annotation { "Feature Type Name" : "Feature", "Feature Type Description" : "" }
export const myFeature = defineFeature(function(context is Context, id is Id, definition is map)
    precondition{}
    {
        {
            var Q0;
            Q0=qCreatedBy(makeId("Top.planeOp"),FACE);
            var sketch = newSketch(context, id + "F0", { "sketchPlane" : qUnion([Q0])});
            skLineSegment(sketch, "E0.bottom", {"start": v(50.8, 25.4) * mm, "end": v(-50.8, 25.4) * mm});
            skLineSegment(sketch, "E0.top", {"start": v(50.8, -25.4) * mm, "end": v(-50.8, -25.4) * mm});
            skLineSegment(sketch, "E0.left", {"start": v(50.8, 25.4) * mm, "end": v(50.8, -25.4) * mm});
            skLineSegment(sketch, "E0.right", {"start": v(-50.8, 25.4) * mm, "end": v(-50.8, -25.4) * mm});
            skPoint(sketch, "E0.middle", {"position": v(0, 0) * mm});
            skSolve(sketch);
        }
        {
            var Q0;
            Q0=makeQuery(id+"F0.imprint","IMPRINT",FACE,{"disambiguationData":[TD([[makeQuery(id+"F0.imprint","IMPRINT",EDGE,{"derivedFrom":sQuery(id+"F0.wireOp",EDGE,"E0.bottom")}),1.0]])]});
            var Q1;
            Q1 = qSketchRegion(id + "F2", true);
            extrude(context, id + "F1", {"entities" : qUnion([Q0, Q1]), "depth" : 6.35 * mm, "offsetDistance" : 25.4 * mm});
        }
        {
            var Q0;
            Q0=makeQuery(id+"F1.opExtrude","CAP_FACE",FACE,{"disambiguationData":[OSD([sQuery(id+"F0.wireOp",EDGE,"E0.bottom"),sQuery(id+"F0.wireOp",EDGE,"E0.top"),sQuery(id+"F0.wireOp",EDGE,"E0.left"),sQuery(id+"F0.wireOp",EDGE,"E0.right")])],"isStart":false});
            var sketch = newSketch(context, id + "F2", { "sketchPlane" : qUnion([Q0])});
            skText(sketch, "E1", { "text": "Michael De Tata", "fontName": "OpenSans-Bold.ttf"});
            const initialGuessF2  = {"E1": [-0.04472, 0.0108, 1, 0, 0.00818]};
            skSetInitialGuess(sketch, initialGuessF2);
            skSolve(sketch);
        }
        {
            var Q0;
            Q0=makeQuery(id+"F2.imprint","IMPRINT",FACE,{"disambiguationData":[TD([[makeQuery(id+"F2.imprint","IMPRINT",EDGE,{"derivedFrom":sQuery(id+"F2.wireOp",EDGE,"E1.sketch_text.stroke-0")}),1.0]])]});
            var sketch = newSketch(context, id + "F3", { "sketchPlane" : qUnion([Q0])});
            skCircle(sketch, "E2", {"center": v(-29.02, -8) * mm, "radius": 11.12 * mm});
            skArc(sketch, "E3", {"start": v(-35.55, 0) * mm, "mid": v(-39.34, -7.67) * mm, "end": v(-36.05, -15.56) * mm});
            skArc(sketch, "E4", {"start": v(-36.05, -15.56) * mm, "mid": v(-35.35, -14.88) * mm, "end": v(-34.72, -14.14) * mm});
            skArc(sketch, "E5", {"start": v(-35.25, -16.23) * mm, "mid": v(-34.54, -15.43) * mm, "end": v(-33.9, -14.58) * mm});
            skArc(sketch, "E6", {"start": v(-22.4, -0.07) * mm, "mid": v(-22.9, -0.63) * mm, "end": v(-23.36, -1.22) * mm});
            skArc(sketch, "E7", {"start": v(-21.73, -0.68) * mm, "mid": v(-22.18, -1.12) * mm, "end": v(-22.6, -1.58) * mm});
            skEllipticalArc(sketch, "E8", {});
            skEllipticalArc(sketch, "E9", {});
            skEllipticalArc(sketch, "E10", {});
            skEllipticalArc(sketch, "E11", {});
            skPoint(sketch, "E11.centerSnap0", {"position": v(-25.24, -8.2) * mm});
            skEllipticalArc(sketch, "E12", {});
            skEllipticalArc(sketch, "E13", {});
            skEllipticalArc(sketch, "E14", {});
            skEllipticalArc(sketch, "E15", {});
            skEllipticalArc(sketch, "E16", {});
            skEllipticalArc(sketch, "E17", {});
            skEllipticalArc(sketch, "E18", {});
            skEllipticalArc(sketch, "E19", {});
            skEllipticalArc(sketch, "E20", {});
            skEllipticalArc(sketch, "E21", {});
            skEllipticalArc(sketch, "E22.trimOffspring", {});
            skArc(sketch, "E23.trimOffspring", {"start": v(-35.16, -0.42) * mm, "mid": v(-35.35, -0.2) * mm, "end": v(-35.55, 0) * mm});
            skArc(sketch, "E24.trimOffspring", {"start": v(-34.26, 0.05) * mm, "mid": v(-34.49, 0.34) * mm, "end": v(-34.72, 0.62) * mm});
            skEllipticalArc(sketch, "E25.trimOffspring", {});
            skArc(sketch, "E26.trimOffspring", {"start": v(-33.09, -1.81) * mm, "mid": v(-33.44, -1.16) * mm, "end": v(-33.84, -0.54) * mm});
            skArc(sketch, "E27.trimOffspring", {"start": v(-33.92, -2.11) * mm, "mid": v(-34.3, -1.53) * mm, "end": v(-34.7, -0.97) * mm});
            skArc(sketch, "E28.trimOffspring", {"start": v(-32.13, -4.31) * mm, "mid": v(-32.42, -3.37) * mm, "end": v(-32.78, -2.45) * mm});
            skArc(sketch, "E29.trimOffspring", {"start": v(-32.91, -4.42) * mm, "mid": v(-33.21, -3.56) * mm, "end": v(-33.59, -2.73) * mm});
            skEllipticalArc(sketch, "E30.trimOffspring", {});
            skArc(sketch, "E31.trimOffspring", {"start": v(-31.72, -6.96) * mm, "mid": v(-31.8, -5.97) * mm, "end": v(-31.97, -4.99) * mm});
            skArc(sketch, "E32.trimOffspring", {"start": v(-32.46, -6.96) * mm, "mid": v(-32.55, -6.03) * mm, "end": v(-32.73, -5.1) * mm});
            skEllipticalArc(sketch, "E33.trimOffspring", {});
            skArc(sketch, "E34.trimOffspring", {"start": v(-32.6, -9.41) * mm, "mid": v(-32.49, -8.52) * mm, "end": v(-32.44, -7.62) * mm});
            skArc(sketch, "E35.trimOffspring", {"start": v(-31.88, -9.55) * mm, "mid": v(-31.76, -8.59) * mm, "end": v(-31.7, -7.61) * mm});
            skEllipticalArc(sketch, "E36.trimOffspring", {});
            skEllipticalArc(sketch, "E37.trimOffspring", {});
            skArc(sketch, "E38.trimOffspring", {"start": v(-33.3, -11.72) * mm, "mid": v(-33, -10.93) * mm, "end": v(-32.76, -10.12) * mm});
            skArc(sketch, "E39.trimOffspring", {"start": v(-32.5, -11.91) * mm, "mid": v(-32.24, -11.11) * mm, "end": v(-32.02, -10.3) * mm});
            skEllipticalArc(sketch, "E40.trimOffspring", {});
            skArc(sketch, "E41.trimOffspring", {"start": v(-34.3, -13.57) * mm, "mid": v(-33.92, -12.96) * mm, "end": v(-33.57, -12.33) * mm});
            skArc(sketch, "E42.trimOffspring", {"start": v(-33.5, -13.95) * mm, "mid": v(-33.12, -13.28) * mm, "end": v(-32.78, -12.59) * mm});
            skEllipticalArc(sketch, "E43.trimOffspring", {});
            skArc(sketch, "E44.trimOffspring", {"start": v(-23.75, -1.78) * mm, "mid": v(-24.13, -2.4) * mm, "end": v(-24.47, -3.03) * mm});
            skArc(sketch, "E45.trimOffspring", {"start": v(-23, -2.08) * mm, "mid": v(-23.42, -2.67) * mm, "end": v(-23.8, -3.28) * mm});
            skEllipticalArc(sketch, "E46.trimOffspring", {});
            skArc(sketch, "E47.trimOffspring", {"start": v(-24.83, -3.8) * mm, "mid": v(-25.1, -4.53) * mm, "end": v(-25.34, -5.28) * mm});
            skArc(sketch, "E48.trimOffspring", {"start": v(-24.17, -3.98) * mm, "mid": v(-24.48, -4.7) * mm, "end": v(-24.75, -5.44) * mm});
            skEllipticalArc(sketch, "E49.trimOffspring", {});
            skArc(sketch, "E50.trimOffspring", {"start": v(-25.55, -6.1) * mm, "mid": v(-25.7, -6.98) * mm, "end": v(-25.79, -7.86) * mm});
            skArc(sketch, "E51.trimOffspring", {"start": v(-24.96, -6.21) * mm, "mid": v(-25.12, -7.03) * mm, "end": v(-25.22, -7.87) * mm});
            skEllipticalArc(sketch, "E52.trimOffspring", {});
            skArc(sketch, "E53.trimOffspring", {"start": v(-25.25, -8.52) * mm, "mid": v(-25.23, -9.53) * mm, "end": v(-25.11, -10.54) * mm});
            skArc(sketch, "E54.trimOffspring", {"start": v(-25.82, -8.52) * mm, "mid": v(-25.79, -9.57) * mm, "end": v(-25.67, -10.61) * mm});
            skEllipticalArc(sketch, "E55.trimOffspring", {});
            skArc(sketch, "E56.trimOffspring", {"start": v(-24.97, -11.27) * mm, "mid": v(-24.73, -12.13) * mm, "end": v(-24.42, -12.98) * mm});
            skArc(sketch, "E57.trimOffspring", {"start": v(-25.54, -11.33) * mm, "mid": v(-25.31, -12.25) * mm, "end": v(-25.01, -13.15) * mm});
            skEllipticalArc(sketch, "E58.trimOffspring", {});
            skArc(sketch, "E59.trimOffspring", {"start": v(-24.14, -13.6) * mm, "mid": v(-23.8, -14.23) * mm, "end": v(-23.43, -14.84) * mm});
            skArc(sketch, "E60.trimOffspring", {"start": v(-24.77, -13.75) * mm, "mid": v(-24.44, -14.45) * mm, "end": v(-24.07, -15.13) * mm});
            skEllipticalArc(sketch, "E61.trimOffspring", {});
            skArc(sketch, "E62.trimOffspring", {"start": v(-23.02, -15.41) * mm, "mid": v(-22.78, -15.73) * mm, "end": v(-22.52, -16.03) * mm});
            skArc(sketch, "E63.trimOffspring", {"start": v(-23.68, -15.74) * mm, "mid": v(-23.42, -16.12) * mm, "end": v(-23.14, -16.49) * mm});
            skArc(sketch, "E64.trimOffspring", {"start": v(-22.4, -0.07) * mm, "mid": v(-28.45, 2.31) * mm, "end": v(-34.72, 0.62) * mm});
            skArc(sketch, "E65.trimOffspring", {"start": v(-22.52, -16.03) * mm, "mid": v(-18.7, -8.53) * mm, "end": v(-21.73, -0.68) * mm});
            skArc(sketch, "E66.trimOffspring", {"start": v(-35.25, -16.23) * mm, "mid": v(-29.24, -18.32) * mm, "end": v(-23.14, -16.49) * mm});
            const initialGuessF3  = {"E8": [-0.023297229781746864, -0.0016107000410556793, 0.9221942343893569, -0.38672702783620916, 0.0013262189090201646, 0.0003399103867390777, 1.7313775885719243, 4.442775066617612], "E9": [-0.024545256048440933, -0.003444293048232794, 0.9558595513992154, -0.2938239574964756, 0.0015029078221081562, 0.0004227233566344582, 1.6047845985919382, 4.6025506559326015], "E10": [-0.025348041206599586, -0.005710541736334137, 0.974924291865179, -0.22253679500518414, 0.0015653299666596133, 0.00042170546441825264, 1.6300234577391468, 4.644150607240461], "E11": [-0.025522032752633095, -0.008192163310697637, 1, 0, 0.0016319900751113892, 0.0003325533746048474, 4.877375785203131, 1.3848873868999396], "E12": [-0.02524203405883331, -0.010927993804216388, 0.9937450408144041, 0.11167270864798855, 0.0014704648821028934, 0.00037379822869026394, 1.8415584680353316, 4.4763722036686], "E13": [-0.024512993171811104, -0.013346818275749683, 0.9701425907691357, 0.2425352625408302, 0.0012090342196172017, 0.0003386781060782523, 1.939812410065906, 4.421933745184485], "E14": [-0.023631859570741653, -0.01531875692307949, 0.9100199085187781, 0.4145645499792218, 0.0013795041764484977, 0.0003653637346890277, 1.8018677319717407, 4.552518399412736], "E15": [-0.03444818779826164, -0.0004427310486789793, 0.8955800676101024, 0.4449003736787423, 0.0014354458638594894, 0.00037730834423175153, 2.022937592477684, 4.385241428417938], "E16": [-0.03332614153623781, -0.0022695872467008976, 0.9465100988838268, 0.3226741897191789, 0.0013755128516680078, 0.0003682691662007112, 1.9552328247544597, 4.42012321917862], "E17": [-0.03250364214181944, -0.004715504590421, 0.9906416472610607, 0.1364885589047379, 0.0015840429664156594, 0.0003628525066166874, 1.8023954855252398, 4.5389323865172075], "E18": [-0.03211632743477267, -0.007288026157766333, 1, 0, 0.0017251316457986832, 0.00033600255318168857, 1.7715815328165256, 4.520976886793743], "E19": [-0.032169036567217014, -0.009877295233307628, 0.978180882111051, -0.20775505257982543, 0.0016113528371813277, 0.0003826132732245725, 1.903385023495256, 4.379874231974156], "E20": [-0.03279896825552073, -0.012205153703689211, 0.9639113213254764, -0.26622352379264724, 0.0015194399101018097, 0.00036448954381331823, 1.9795308566801448, 4.225214624885279], "E21": [-0.033999312669038134, -0.014110893011093573, 0.9026662996091727, -0.4303412036394881, 0.0013289304469737081, 0.00038306743312276623, 1.9598946097063568, 4.21503529249235], "E22.trimOffspring": [-0.03444818779826164, -0.0004427310486789793, 0.8955800676101024, 0.4449003736787423, 0.0014354458638594894, 0.00037730834423175153, 5.069920585606974, 1.2984009443078852], "E25.trimOffspring": [-0.03332614153623781, -0.0022695872467008976, 0.9465100988838268, 0.3226741897191789, 0.0013755128516680078, 0.0003682691662007112, 5.05048796778761, 1.2956370615444666], "E30.trimOffspring": [-0.03250364214181944, -0.004715504590421, 0.9906416472610607, 0.1364885589047379, 0.0015840429664156594, 0.0003628525066166874, 5.029190785969994, 1.2974556023185868], "E33.trimOffspring": [-0.03211632743477267, -0.007288026157766333, 1, 0, 0.0017251316457986832, 0.00033600255318168857, 4.950210489805461, 1.3401253138698446], "E36.trimOffspring": [-0.032169036567217014, -0.009877295233307628, 0.978180882111051, -0.20775505257982543, 0.0016113528371813277, 0.0003826132732245725, 4.855897131174967, 1.4346116706158747], "E37.trimOffspring": [-0.03279896825552073, -0.012205153703689211, 0.9639113213254764, -0.26622352379264724, 0.0015194399101018097, 0.00036448954381331823, 4.788924618250473, 1.4369349986347975], "E40.trimOffspring": [-0.033999312669038134, -0.014110893011093573, 0.9026662996091727, -0.4303412036394881, 0.0013289304469737081, 0.00038306743312276623, 4.936684034247733, 1.273865923141645], "E43.trimOffspring": [-0.023297229781746864, -0.0016107000410556793, 0.9221942343893569, -0.38672702783620916, 0.0013262189090201646, 0.0003399103867390777, 5.058956423378174, 1.0757933932276291], "E46.trimOffspring": [-0.024545256048440933, -0.003444293048232794, 0.9558595513992154, -0.2938239574964756, 0.0015029078221081562, 0.0004227233566344582, 5.064677294631309, 1.1127932101347984], "E49.trimOffspring": [-0.025348041206599586, -0.005710541736334137, 0.974924291865179, -0.22253679500518414, 0.0015653299666596133, 0.00042170546441825264, 5.031559149779341, 1.2274527694819934], "E52.trimOffspring": [-0.025522032752633095, -0.008192163310697637, 1, 0, 0.0016319900751113892, 0.0003325533746048474, 1.7356086307068754, 4.5309761465529315], "E55.trimOffspring": [-0.02524203405883331, -0.010927993804216388, 0.9937450408144041, 0.11167270864798855, 0.0014704648821028934, 0.00037379822869026394, 4.872981376554883, 1.4529925075761783], "E58.trimOffspring": [-0.024512993171811104, -0.013346818275749683, 0.9701425907691357, 0.2425352625408302, 0.0012090342196172017, 0.0003386781060782523, 4.964215526835341, 1.4197028482985121], "E61.trimOffspring": [-0.023631859570741653, -0.01531875692307949, 0.9100199085187781, 0.4145645499792218, 0.0013795041764484977, 0.0003653637346890277, 5.094922816644008, 1.2891328392718011]};
            skSetInitialGuess(sketch, initialGuessF3);
            skSolve(sketch);
        }
        {
            var Q0;
            Q0 = qSketchRegion(id + "F3", true);
            extrude(context, id + "F4", {"entities" : qUnion([Q0]), "operationType" : NewBodyOperationType.ADD, "depth" : 3.17 * mm, "offsetDistance" : 25.4 * mm});
        }
        {
            var Q0;
            Q0=makeQuery(id+"F1.opExtrude","CAP_FACE",FACE,{"disambiguationData":[OSD([sQuery(id+"F0.wireOp",EDGE,"E0.bottom"),sQuery(id+"F0.wireOp",EDGE,"E0.top"),sQuery(id+"F0.wireOp",EDGE,"E0.left"),sQuery(id+"F0.wireOp",EDGE,"E0.right")])],"isStart":false});
            var sketch = newSketch(context, id + "F5", { "sketchPlane" : qUnion([Q0])});
            skArc(sketch, "E67", {"start": v(5.27, -19.2) * mm, "mid": v(8.48, -19.92) * mm, "end": v(11.75, -19.65) * mm});
            skArc(sketch, "E68", {"start": v(25.2, 1.07) * mm, "mid": v(21.99, 1.76) * mm, "end": v(18.72, 1.48) * mm});
            skArc(sketch, "E69", {"start": v(25.82, -5.72) * mm, "mid": v(26.07, -2.27) * mm, "end": v(25.2, 1.07) * mm});
            skArc(sketch, "E70", {"start": v(17.08, 1.07) * mm, "mid": v(9.04, -3.02) * mm, "end": v(4.87, -11.01) * mm});
            skArc(sketch, "E71", {"start": v(13.27, -19.46) * mm, "mid": v(21.33, -15.34) * mm, "end": v(25.48, -7.3) * mm});
            skLineSegment(sketch, "E72", {"start": v(18.04, -5.49) * mm, "end": v(18.72, -4.8) * mm});
            skArc(sketch, "E73", {"start": v(19.63, -5.59) * mm, "mid": v(19.54, -4.77) * mm, "end": v(18.72, -4.8) * mm});
            skLineSegment(sketch, "E74", {"start": v(19.63, -5.59) * mm, "end": v(18.9, -6.34) * mm});
            skLineSegment(sketch, "E75", {"start": v(18.9, -6.34) * mm, "end": v(19.85, -7.25) * mm});
            skArc(sketch, "E76", {"start": v(18.93, -8.27) * mm, "mid": v(19.73, -8.07) * mm, "end": v(19.85, -7.25) * mm});
            skLineSegment(sketch, "E77", {"start": v(17.97, -7.27) * mm, "end": v(18.93, -8.27) * mm});
            skLineSegment(sketch, "E78", {"start": v(17.97, -7.27) * mm, "end": v(17.06, -8.16) * mm});
            skLineSegment(sketch, "E79", {"start": v(17.06, -8.16) * mm, "end": v(17.94, -9.07) * mm});
            skArc(sketch, "E80", {"start": v(17.09, -10.12) * mm, "mid": v(17.9, -9.9) * mm, "end": v(17.94, -9.07) * mm});
            skLineSegment(sketch, "E81", {"start": v(17.09, -10.12) * mm, "end": v(16.14, -9.17) * mm});
            skLineSegment(sketch, "E82", {"start": v(16.14, -9.17) * mm, "end": v(15.18, -10.12) * mm});
            skLineSegment(sketch, "E83", {"start": v(15.18, -10.12) * mm, "end": v(15.96, -10.9) * mm});
            skArc(sketch, "E84", {"start": v(15.15, -11.9) * mm, "mid": v(16, -11.76) * mm, "end": v(15.96, -10.9) * mm});
            skLineSegment(sketch, "E85", {"start": v(15.15, -11.9) * mm, "end": v(14.3, -11) * mm});
            skLineSegment(sketch, "E86", {"start": v(14.3, -11) * mm, "end": v(13.34, -11.9) * mm});
            skLineSegment(sketch, "E87", {"start": v(13.34, -11.9) * mm, "end": v(14.15, -12.75) * mm});
            skArc(sketch, "E88", {"start": v(13.17, -13.64) * mm, "mid": v(14.1, -13.7) * mm, "end": v(14.15, -12.75) * mm});
            skLineSegment(sketch, "E89", {"start": v(13.17, -13.64) * mm, "end": v(12.44, -12.89) * mm});
            skLineSegment(sketch, "E90", {"start": v(12.44, -12.89) * mm, "end": v(11.81, -13.64) * mm});
            skArc(sketch, "E91", {"start": v(10.8, -12.59) * mm, "mid": v(10.91, -13.5) * mm, "end": v(11.81, -13.64) * mm});
            skLineSegment(sketch, "E92", {"start": v(10.8, -12.59) * mm, "end": v(11.54, -11.9) * mm});
            skLineSegment(sketch, "E93", {"start": v(11.54, -11.9) * mm, "end": v(10.55, -11.02) * mm});
            skArc(sketch, "E94", {"start": v(11.55, -10.13) * mm, "mid": v(10.7, -10.17) * mm, "end": v(10.55, -11.02) * mm});
            skLineSegment(sketch, "E95", {"start": v(11.55, -10.13) * mm, "end": v(12.4, -11) * mm});
            skLineSegment(sketch, "E96", {"start": v(12.4, -11) * mm, "end": v(13.3, -10.13) * mm});
            skLineSegment(sketch, "E97", {"start": v(13.3, -10.13) * mm, "end": v(12.4, -9.21) * mm});
            skArc(sketch, "E98", {"start": v(13.46, -8.3) * mm, "mid": v(12.56, -8.32) * mm, "end": v(12.4, -9.21) * mm});
            skLineSegment(sketch, "E99", {"start": v(13.46, -8.3) * mm, "end": v(14.27, -9.15) * mm});
            skLineSegment(sketch, "E100", {"start": v(14.27, -9.15) * mm, "end": v(15.22, -8.24) * mm});
            skLineSegment(sketch, "E101", {"start": v(15.22, -8.24) * mm, "end": v(14.24, -7.33) * mm});
            skArc(sketch, "E102", {"start": v(15.29, -6.44) * mm, "mid": v(14.4, -6.47) * mm, "end": v(14.24, -7.33) * mm});
            skLineSegment(sketch, "E103", {"start": v(15.29, -6.44) * mm, "end": v(16.1, -7.28) * mm});
            skLineSegment(sketch, "E104", {"start": v(16.1, -7.28) * mm, "end": v(17, -6.44) * mm});
            skLineSegment(sketch, "E105", {"start": v(17, -6.44) * mm, "end": v(16.15, -5.55) * mm});
            skArc(sketch, "E106", {"start": v(17.15, -4.67) * mm, "mid": v(16.2, -4.6) * mm, "end": v(16.15, -5.55) * mm});
            skLineSegment(sketch, "E107", {"start": v(17.15, -4.67) * mm, "end": v(18.04, -5.49) * mm});
            skArc(sketch, "E108", {"start": v(4.6, -12.51) * mm, "mid": v(4.31, -15.92) * mm, "end": v(5.27, -19.2) * mm});
            skLineSegment(sketch, "E109", {"start": v(4.87, -11.01) * mm, "end": v(4.6, -12.51) * mm});
            skLineSegment(sketch, "E110", {"start": v(13.27, -19.46) * mm, "end": v(11.75, -19.65) * mm});
            skLineSegment(sketch, "E111", {"start": v(25.82, -5.72) * mm, "end": v(25.48, -7.3) * mm});
            skLineSegment(sketch, "E112", {"start": v(18.72, 1.48) * mm, "end": v(17.08, 1.07) * mm});
            skPoint(sketch, "E113.orphan", {"position": v(17.97, -9.1) * mm});
            skSolve(sketch);
        }
        {
            var Q0;
            Q0 = qSketchRegion(id + "F5", true);
            extrude(context, id + "F6", {"entities" : qUnion([Q0]), "operationType" : NewBodyOperationType.ADD, "depth" : 2.54 * mm, "offsetDistance" : 25.4 * mm});
        }
        {
            var Q0;
            Q0 = qSketchRegion(id + "F2", true);
            extrude(context, id + "F7", {"entities" : qUnion([Q0]), "operationType" : NewBodyOperationType.REMOVE, "oppositeDirection" : true, "depth" : 3.17 * mm, "offsetDistance" : 25.4 * mm});
        }
    });